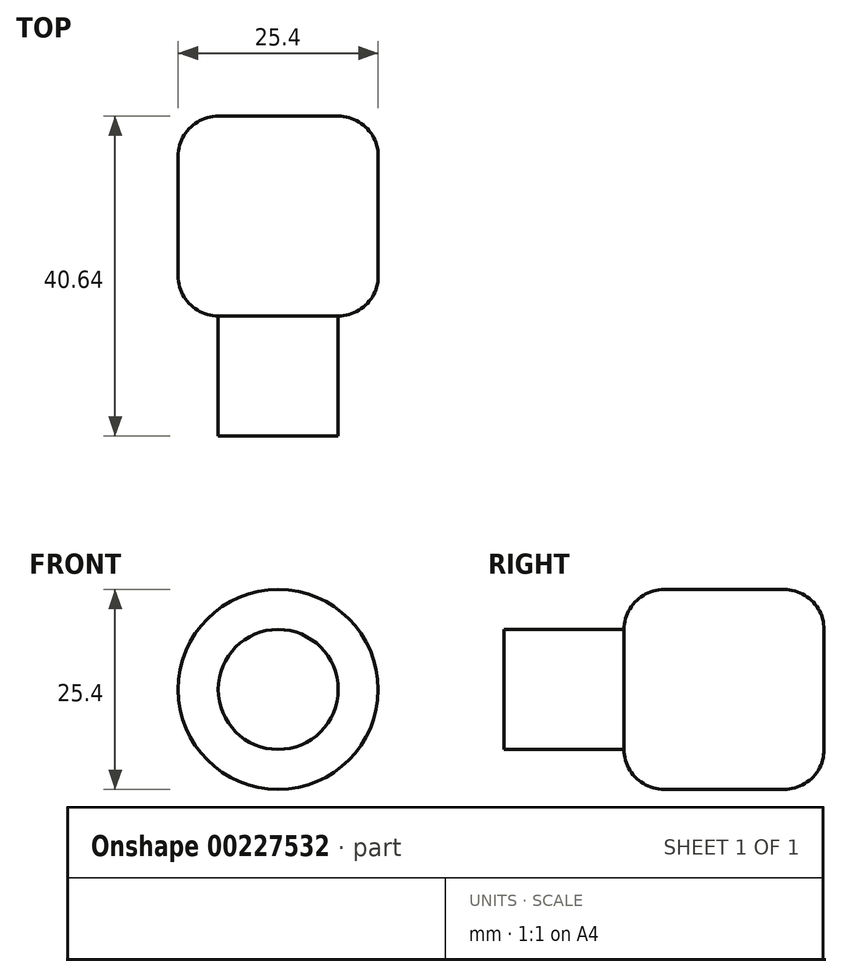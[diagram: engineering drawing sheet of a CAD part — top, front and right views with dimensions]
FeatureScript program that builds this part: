
annotation { "Feature Type Name" : "Feature", "Feature Type Description" : "" }
export const myFeature = defineFeature(function(context is Context, id is Id, definition is map)
    precondition{}
    {
        {
            var Q0;
            Q0=qCreatedBy(makeId("Front.planeOp"),FACE);
            var sketch = newSketch(context, id + "F0", { "sketchPlane" : qUnion([Q0])});
            skCircle(sketch, "E0", {"center": v(0, 0) * mm, "radius": 12.7 * mm});
            skSolve(sketch);
        }
        {
            var Q0;
            Q0=qSketchRegion(id+"F0",true);
            extrude(context, id + "F1", {"entities" : qUnion([Q0]), "depth" : 25.4 * mm});
        }
        {
            var Q0;
            Q0=makeQuery(id+"F1.opExtrude","CAP_EDGE",EDGE,{"disambiguationData":[OSD([sQuery(id+"F0.wireOp",EDGE,"E0")])],"isStart":false});
            var Q1;
            Q1=makeQuery(id+"F1.opExtrude","CAP_EDGE",EDGE,{"disambiguationData":[OSD([sQuery(id+"F0.wireOp",EDGE,"E0")])],"isStart":true});
            fillet(context, id + "F2", {"entities" : qUnion([Q0, Q1]), "radius" : 5.08 * mm, "tangentPropagation" : true, "allowEdgeOverflow" : false});
        }
        {
            var Q0;
            Q0=qCreatedBy(makeId("Front.planeOp"),FACE);
            var sketch = newSketch(context, id + "F3", { "sketchPlane" : qUnion([Q0])});
            skCircle(sketch, "E1", {"center": v(0, 0) * mm, "radius": 6.35 * mm});
            skSolve(sketch);
        }
        {
            var Q0;
            Q0=qSketchRegion(id+"F3",true);
            var Q1;
            Q1=makeQuery(id+"F1.opExtrude","CAP_FACE",FACE,{"disambiguationData":[OSD([sQuery(id+"F0.wireOp",EDGE,"E0")])],"isStart":false});
            extrude(context, id + "F4", {"entities" : qUnion([Q0, Q1]), "operationType" : NewBodyOperationType.ADD, "depth" : 15.24 * mm});
        }
    });
